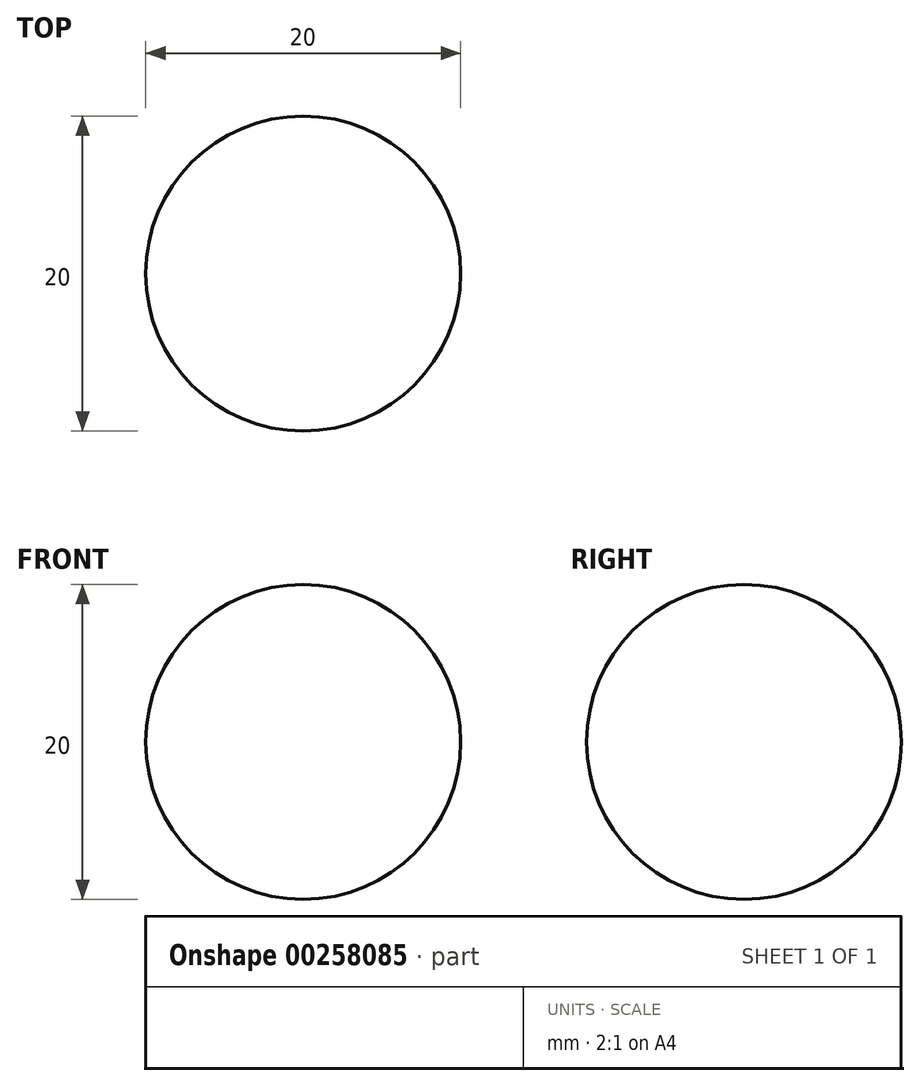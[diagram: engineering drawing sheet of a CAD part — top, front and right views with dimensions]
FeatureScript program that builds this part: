
annotation { "Feature Type Name" : "Feature", "Feature Type Description" : "" }
export const myFeature = defineFeature(function(context is Context, id is Id, definition is map)
    precondition{}
    {
        {
            var Q0;
            Q0=qCreatedBy(makeId("Front.planeOp"),FACE);
            var sketch = newSketch(context, id + "F0", { "sketchPlane" : qUnion([Q0])});
            skArc(sketch, "E0", {"start": v(0, 10) * mm, "mid": v(10, 0) * mm, "end": v(0, -10) * mm});
            skLineSegment(sketch, "E1", {"start": v(0, 10) * mm, "end": v(0, -10) * mm});
            skSolve(sketch);
        }
        {
            var Q0;
            Q0 = qSketchRegion(id + "F0", true);
            var Q1;
            Q1=sQuery(id+"F0.wireOp",EDGE,"E1");
            revolve(context, id + "F1", {"entities" : qUnion([Q0]), "axis" : qUnion([Q1]), "revolveType" : RevolveType.FULL});
        }
    });
